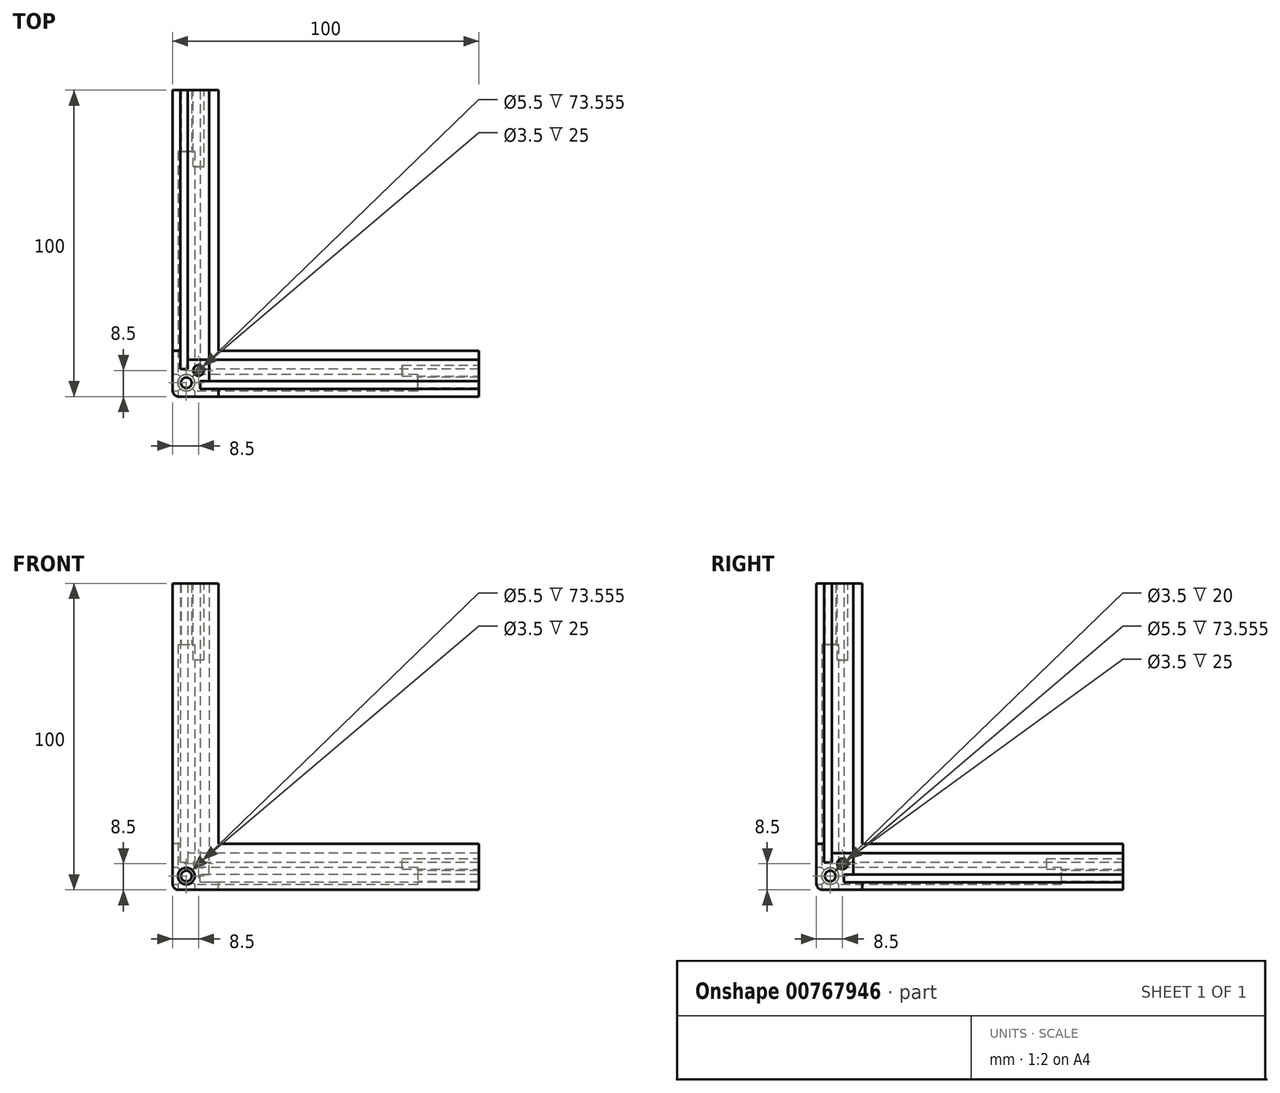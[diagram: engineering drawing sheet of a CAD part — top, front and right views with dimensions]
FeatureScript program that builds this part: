
annotation { "Feature Type Name" : "Feature", "Feature Type Description" : "" }
export const myFeature = defineFeature(function(context is Context, id is Id, definition is map)
    precondition{}
    {
        {
            var Q0;
            Q0=qCreatedBy(makeId("Top.planeOp"),FACE);
            var sketch = newSketch(context, id + "F0", { "sketchPlane" : qUnion([Q0])});
            skLineSegment(sketch, "E0", {"start": v(0, 15) * mm, "end": v(0, 0) * mm});
            skLineSegment(sketch, "E1", {"start": v(0, 0) * mm, "end": v(15, 0) * mm});
            skLineSegment(sketch, "E2", {"start": v(15, 0) * mm, "end": v(15, 2.5) * mm});
            skLineSegment(sketch, "E3", {"start": v(15, 2.5) * mm, "end": v(9, 2.5) * mm});
            skLineSegment(sketch, "E4", {"start": v(9, 2.5) * mm, "end": v(9, 5) * mm});
            skLineSegment(sketch, "E5", {"start": v(9, 5) * mm, "end": v(12, 5) * mm});
            skLineSegment(sketch, "E6", {"start": v(12, 5) * mm, "end": v(12, 12) * mm});
            skLineSegment(sketch, "E7", {"start": v(12, 12) * mm, "end": v(5, 12) * mm});
            skLineSegment(sketch, "E8", {"start": v(5, 12) * mm, "end": v(5, 9) * mm});
            skLineSegment(sketch, "E9", {"start": v(5, 9) * mm, "end": v(2.5, 9) * mm});
            skLineSegment(sketch, "E10", {"start": v(2.5, 9) * mm, "end": v(2.5, 15) * mm});
            skLineSegment(sketch, "E11", {"start": v(2.5, 15) * mm, "end": v(0, 15) * mm});
            skLineSegment(sketch, "E12", {"start": v(9, 5) * mm, "end": v(9, 9) * mm, "construction": true});
            skLineSegment(sketch, "E13", {"start": v(9, 9) * mm, "end": v(5, 9) * mm, "construction": true});
            skLineSegment(sketch, "E14", {"start": v(2.5, 9) * mm, "end": v(0, 9) * mm, "construction": true});
            skLineSegment(sketch, "E15", {"start": v(9, 2.5) * mm, "end": v(9, 0) * mm, "construction": true});
            skLineSegment(sketch, "E16", {"start": v(9, 0) * mm, "end": v(0, 9) * mm, "construction": true});
            skLineSegment(sketch, "E17", {"start": v(0, 0) * mm, "end": v(9, 9) * mm, "construction": true});
            skCircle(sketch, "E18", {"center": v(4.5, 4.5) * mm, "radius": 1.75 * mm});
            skSolve(sketch);
        }
        {
            var Q0;
            Q0=makeQuery(id+"F0.imprint","IMPRINT",FACE,{"disambiguationData":[TD([[makeQuery(id+"F0.imprint","IMPRINT",EDGE,{"derivedFrom":sQuery(id+"F0.wireOp",EDGE,"E0")}),1.0]])]});
            extrude(context, id + "F1", {"entities" : qUnion([Q0]), "depth" : 100 * mm, "offsetDistance" : 25 * mm});
        }
        {
            var Q0;
            Q0=qCreatedBy(makeId("Right.planeOp"),FACE);
            var sketch = newSketch(context, id + "F2", { "sketchPlane" : qUnion([Q0])});
            skLineSegment(sketch, "E19", {"start": v(0, 15) * mm, "end": v(0, 0) * mm});
            skLineSegment(sketch, "E20", {"start": v(0, 0) * mm, "end": v(15, 0) * mm});
            skLineSegment(sketch, "E21", {"start": v(15, 0) * mm, "end": v(15, 2.5) * mm});
            skLineSegment(sketch, "E22", {"start": v(15, 2.5) * mm, "end": v(9, 2.5) * mm});
            skLineSegment(sketch, "E23", {"start": v(9, 2.5) * mm, "end": v(9, 5) * mm});
            skLineSegment(sketch, "E24", {"start": v(9, 5) * mm, "end": v(12, 5) * mm});
            skLineSegment(sketch, "E25", {"start": v(12, 5) * mm, "end": v(12, 12) * mm});
            skLineSegment(sketch, "E26", {"start": v(12, 12) * mm, "end": v(5, 12) * mm});
            skLineSegment(sketch, "E27", {"start": v(5, 12) * mm, "end": v(5, 9) * mm});
            skLineSegment(sketch, "E28", {"start": v(5, 9) * mm, "end": v(2.5, 9) * mm});
            skLineSegment(sketch, "E29", {"start": v(2.5, 9) * mm, "end": v(2.5, 15) * mm});
            skLineSegment(sketch, "E30", {"start": v(2.5, 15) * mm, "end": v(0, 15) * mm});
            skLineSegment(sketch, "E31", {"start": v(9, 5) * mm, "end": v(9, 9) * mm, "construction": true});
            skLineSegment(sketch, "E32", {"start": v(9, 9) * mm, "end": v(5, 9) * mm, "construction": true});
            skLineSegment(sketch, "E33", {"start": v(2.5, 9) * mm, "end": v(0.02, 9) * mm, "construction": true});
            skLineSegment(sketch, "E34", {"start": v(9, 2.5) * mm, "end": v(9, 0) * mm, "construction": true});
            skLineSegment(sketch, "E35", {"start": v(9, 0) * mm, "end": v(0.02, 9) * mm, "construction": true});
            skLineSegment(sketch, "E36", {"start": v(0, 0) * mm, "end": v(9, 9) * mm, "construction": true});
            skCircle(sketch, "E37", {"center": v(4.5, 4.5) * mm, "radius": 1.75 * mm});
            skSolve(sketch);
        }
        {
            var Q0;
            Q0 = qSketchRegion(id + "F2", true);
            extrude(context, id + "F3", {"entities" : qUnion([Q0]), "operationType" : NewBodyOperationType.ADD, "depth" : 100 * mm, "offsetDistance" : 25 * mm});
        }
        {
            var Q0;
            Q0=qCreatedBy(makeId("Front.planeOp"),FACE);
            var sketch = newSketch(context, id + "F4", { "sketchPlane" : qUnion([Q0])});
            skLineSegment(sketch, "E38", {"start": v(0, 15) * mm, "end": v(0, 0) * mm});
            skLineSegment(sketch, "E39", {"start": v(0, 0) * mm, "end": v(15, 0) * mm});
            skLineSegment(sketch, "E40", {"start": v(15, 0) * mm, "end": v(15, 2.5) * mm});
            skLineSegment(sketch, "E41", {"start": v(15, 2.5) * mm, "end": v(9, 2.5) * mm});
            skLineSegment(sketch, "E42", {"start": v(9, 2.5) * mm, "end": v(9, 5) * mm});
            skLineSegment(sketch, "E43", {"start": v(9, 5) * mm, "end": v(12, 5) * mm});
            skLineSegment(sketch, "E44", {"start": v(12, 5) * mm, "end": v(12, 12) * mm});
            skLineSegment(sketch, "E45", {"start": v(12, 12) * mm, "end": v(5, 12) * mm});
            skLineSegment(sketch, "E46", {"start": v(5, 12) * mm, "end": v(5, 9) * mm});
            skLineSegment(sketch, "E47", {"start": v(5, 9) * mm, "end": v(2.5, 9) * mm});
            skLineSegment(sketch, "E48", {"start": v(2.5, 9) * mm, "end": v(2.5, 15) * mm});
            skLineSegment(sketch, "E49", {"start": v(2.5, 15) * mm, "end": v(0, 15) * mm});
            skLineSegment(sketch, "E50", {"start": v(9, 5) * mm, "end": v(9, 9) * mm, "construction": true});
            skLineSegment(sketch, "E51", {"start": v(9, 9) * mm, "end": v(5, 9) * mm, "construction": true});
            skLineSegment(sketch, "E52", {"start": v(2.5, 9) * mm, "end": v(0, 9) * mm, "construction": true});
            skLineSegment(sketch, "E53", {"start": v(9, 2.5) * mm, "end": v(9, 0) * mm, "construction": true});
            skLineSegment(sketch, "E54", {"start": v(9, 0) * mm, "end": v(0, 9) * mm, "construction": true});
            skLineSegment(sketch, "E55", {"start": v(0, 0) * mm, "end": v(9, 9) * mm, "construction": true});
            skCircle(sketch, "E56", {"center": v(4.5, 4.5) * mm, "radius": 1.75 * mm});
            skSolve(sketch);
        }
        {
            var Q0;
            Q0 = qSketchRegion(id + "F4", true);
            extrude(context, id + "F5", {"entities" : qUnion([Q0]), "operationType" : NewBodyOperationType.ADD, "oppositeDirection" : true, "depth" : 100 * mm, "offsetDistance" : 25 * mm});
        }
        {
            var Q0;
            {var subQ0=makeQuery(id+"F3.opExtrude","SWEPT_FACE",FACE,{"disambiguationData":[OSD([sQuery(id+"F2.wireOp",EDGE,"E25")])]});var subQ1=makeQuery(id+"F1.opExtrude","SWEPT_FACE",FACE,{"disambiguationData":[OSD([sQuery(id+"F0.wireOp",EDGE,"E7")])]});Q0=makeQuery(id+"F5.boolean.opBoolean","SPLIT",FACE,{"disambiguationData":[TD([makeQuery(id+"F1.opExtrude","SWEPT_FACE",FACE,{"disambiguationData":[OSD([sQuery(id+"F0.wireOp",EDGE,"E10")])]})])],"derivedFrom":makeQuery(id+"F3.boolean.opBoolean","MERGE",FACE,{"derivedFrom":[subQ1,subQ0]})});}
            extrude(context, id + "F6", {"entities" : qUnion([Q0]), "operationType" : NewBodyOperationType.REMOVE, "oppositeDirection" : true, "depth" : 3 * mm, "offsetDistance" : 25 * mm});
        }
        {
            var Q0;
            Q0=makeQuery(id+"F5.boolean.opBoolean","SPLIT",FACE,{"disambiguationData":[TD([makeQuery(id+"F1.opExtrude","SWEPT_FACE",FACE,{"disambiguationData":[OSD([sQuery(id+"F0.wireOp",EDGE,"E3")])]})])],"derivedFrom":makeQuery(id+"F5.opExtrude","SWEPT_FACE",FACE,{"disambiguationData":[OSD([sQuery(id+"F4.wireOp",EDGE,"E44")])]})});
            extrude(context, id + "F7", {"entities" : qUnion([Q0]), "operationType" : NewBodyOperationType.REMOVE, "oppositeDirection" : true, "depth" : 3 * mm, "offsetDistance" : 25 * mm});
        }
        {
            var Q0;
            Q0=makeQuery(id+"F3.boolean.opBoolean","SPLIT",FACE,{"disambiguationData":[TD([makeQuery(id+"F3.opExtrude","SWEPT_FACE",FACE,{"disambiguationData":[OSD([sQuery(id+"F2.wireOp",EDGE,"E22")])]})])],"derivedFrom":makeQuery(id+"F1.opExtrude","SWEPT_FACE",FACE,{"disambiguationData":[OSD([sQuery(id+"F0.wireOp",EDGE,"E6")])]})});
            extrude(context, id + "F8", {"entities" : qUnion([Q0]), "operationType" : NewBodyOperationType.REMOVE, "oppositeDirection" : true, "depth" : 3 * mm, "offsetDistance" : 25 * mm});
        }
        {
            var Q0;
            Q0=makeQuery(id+"F5.boolean.opBoolean","MERGE",FACE,{"derivedFrom":[makeQuery(id+"F1.opExtrude","SWEPT_FACE",FACE,{"disambiguationData":[OSD([sQuery(id+"F0.wireOp",EDGE,"E0")])]}),makeQuery(id+"F5.opExtrude","SWEPT_FACE",FACE,{"disambiguationData":[OSD([sQuery(id+"F4.wireOp",EDGE,"E38")])]})]});
            var sketch = newSketch(context, id + "F9", { "sketchPlane" : qUnion([Q0])});
            skCircle(sketch, "E57", {"center": v(-4.5, 4.5) * mm, "radius": 2.75 * mm});
            skSolve(sketch);
        }
        {
            var Q0;
            Q0 = qSketchRegion(id + "F9", true);
            extrude(context, id + "F10", {"entities" : qUnion([Q0]), "operationType" : NewBodyOperationType.REMOVE, "oppositeDirection" : true, "depth" : 80 * mm, "offsetDistance" : 25 * mm});
        }
        {
            var Q0;
            Q0=makeQuery(id+"F5.boolean.opBoolean","MERGE",FACE,{"derivedFrom":[makeQuery(id+"F3.boolean.opBoolean","MERGE",FACE,{"derivedFrom":[makeQuery(id+"F1.opExtrude","CAP_FACE",FACE,{"disambiguationData":[OSD([sQuery(id+"F0.wireOp",EDGE,"E0"),sQuery(id+"F0.wireOp",EDGE,"E1"),sQuery(id+"F0.wireOp",EDGE,"E2"),sQuery(id+"F0.wireOp",EDGE,"E3"),sQuery(id+"F0.wireOp",EDGE,"E4"),sQuery(id+"F0.wireOp",EDGE,"E5"),sQuery(id+"F0.wireOp",EDGE,"E6"),sQuery(id+"F0.wireOp",EDGE,"E7"),sQuery(id+"F0.wireOp",EDGE,"E8"),sQuery(id+"F0.wireOp",EDGE,"E9"),sQuery(id+"F0.wireOp",EDGE,"E10"),sQuery(id+"F0.wireOp",EDGE,"E11"),sQuery(id+"F0.wireOp",EDGE,"E18")])],"isStart":true}),makeQuery(id+"F3.opExtrude","SWEPT_FACE",FACE,{"disambiguationData":[OSD([sQuery(id+"F2.wireOp",EDGE,"E20")])]})]}),makeQuery(id+"F5.opExtrude","SWEPT_FACE",FACE,{"disambiguationData":[OSD([sQuery(id+"F4.wireOp",EDGE,"E39")])]})]});
            var sketch = newSketch(context, id + "F11", { "sketchPlane" : qUnion([Q0])});
            skCircle(sketch, "E58", {"center": v(4.5, -4.5) * mm, "radius": 2.75 * mm});
            skSolve(sketch);
        }
        {
            var Q0;
            Q0 = qSketchRegion(id + "F11", true);
            extrude(context, id + "F12", {"entities" : qUnion([Q0]), "operationType" : NewBodyOperationType.REMOVE, "oppositeDirection" : true, "depth" : 80 * mm, "offsetDistance" : 25 * mm});
        }
        {
            var Q0;
            Q0=makeQuery(id+"F3.boolean.opBoolean","MERGE",FACE,{"derivedFrom":[makeQuery(id+"F1.opExtrude","SWEPT_FACE",FACE,{"disambiguationData":[OSD([sQuery(id+"F0.wireOp",EDGE,"E1")])]}),makeQuery(id+"F3.opExtrude","SWEPT_FACE",FACE,{"disambiguationData":[OSD([sQuery(id+"F2.wireOp",EDGE,"E19")])]})]});
            var sketch = newSketch(context, id + "F13", { "sketchPlane" : qUnion([Q0])});
            skCircle(sketch, "E59", {"center": v(4.5, 4.5) * mm, "radius": 2.75 * mm});
            skSolve(sketch);
        }
        {
            var Q0;
            Q0 = qSketchRegion(id + "F13", true);
            extrude(context, id + "F14", {"entities" : qUnion([Q0]), "operationType" : NewBodyOperationType.REMOVE, "oppositeDirection" : true, "depth" : 80 * mm, "offsetDistance" : 25 * mm});
        }
        {
            var Q0;
            Q0=makeQuery(id+"F5.boolean.opBoolean","MERGE",EDGE,{"derivedFrom":[makeQuery(id+"F1.opExtrude","CAP_EDGE",EDGE,{"disambiguationData":[OSD([sQuery(id+"F0.wireOp",EDGE,"E0")])],"isStart":true}),makeQuery(id+"F5.opExtrude","SWEPT_EDGE",EDGE,{"disambiguationData":[OSD([sQuery(id+"F4.wireOp",EDGE,"E38"),sQuery(id+"F4.wireOp",EDGE,"E39")])]})]});
            var Q1;
            Q1=makeQuery(id+"F3.boolean.opBoolean","MERGE",EDGE,{"derivedFrom":[makeQuery(id+"F1.opExtrude","CAP_EDGE",EDGE,{"disambiguationData":[OSD([sQuery(id+"F0.wireOp",EDGE,"E1")])],"isStart":true}),makeQuery(id+"F3.opExtrude","SWEPT_EDGE",EDGE,{"disambiguationData":[OSD([sQuery(id+"F2.wireOp",EDGE,"E19"),sQuery(id+"F2.wireOp",EDGE,"E20")])]})]});
            var Q2;
            Q2=makeQuery(id+"F1.opExtrude","SWEPT_EDGE",EDGE,{"disambiguationData":[OSD([sQuery(id+"F0.wireOp",EDGE,"E0"),sQuery(id+"F0.wireOp",EDGE,"E1")])]});
            fillet(context, id + "F15", {"entities" : qUnion([Q0, Q1, Q2]), "radius" : 2 * mm, "tangentPropagation" : true, "allowEdgeOverflow" : false});
        }
        {
            var Q0;
            Q0=makeQuery(id+"F3.opExtrude","CAP_FACE",FACE,{"disambiguationData":[OSD([sQuery(id+"F2.wireOp",EDGE,"E19"),sQuery(id+"F2.wireOp",EDGE,"E20"),sQuery(id+"F2.wireOp",EDGE,"E21"),sQuery(id+"F2.wireOp",EDGE,"E22"),sQuery(id+"F2.wireOp",EDGE,"E23"),sQuery(id+"F2.wireOp",EDGE,"E24"),sQuery(id+"F2.wireOp",EDGE,"E25"),sQuery(id+"F2.wireOp",EDGE,"E26"),sQuery(id+"F2.wireOp",EDGE,"E27"),sQuery(id+"F2.wireOp",EDGE,"E28"),sQuery(id+"F2.wireOp",EDGE,"E29"),sQuery(id+"F2.wireOp",EDGE,"E30"),sQuery(id+"F2.wireOp",EDGE,"E37")])],"isStart":false});
            var sketch = newSketch(context, id + "F16", { "sketchPlane" : qUnion([Q0])});
            skCircle(sketch, "E60", {"center": v(8.5, 8.5) * mm, "radius": 1.75 * mm});
            skLineSegment(sketch, "E61", {"start": v(12, 5) * mm, "end": v(5, 12) * mm, "construction": true});
            skLineSegment(sketch, "E62", {"start": v(12, 12) * mm, "end": v(8.5, 8.5) * mm, "construction": true});
            skSolve(sketch);
        }
        {
            var Q0;
            Q0 = qSketchRegion(id + "F16", true);
            extrude(context, id + "F17", {"entities" : qUnion([Q0]), "operationType" : NewBodyOperationType.REMOVE, "oppositeDirection" : true, "depth" : 25 * mm, "offsetDistance" : 25 * mm});
        }
        {
            var Q0;
            Q0=makeQuery(id+"F1.opExtrude","CAP_FACE",FACE,{"disambiguationData":[OSD([sQuery(id+"F0.wireOp",EDGE,"E0"),sQuery(id+"F0.wireOp",EDGE,"E1"),sQuery(id+"F0.wireOp",EDGE,"E2"),sQuery(id+"F0.wireOp",EDGE,"E3"),sQuery(id+"F0.wireOp",EDGE,"E4"),sQuery(id+"F0.wireOp",EDGE,"E5"),sQuery(id+"F0.wireOp",EDGE,"E6"),sQuery(id+"F0.wireOp",EDGE,"E7"),sQuery(id+"F0.wireOp",EDGE,"E8"),sQuery(id+"F0.wireOp",EDGE,"E9"),sQuery(id+"F0.wireOp",EDGE,"E10"),sQuery(id+"F0.wireOp",EDGE,"E11"),sQuery(id+"F0.wireOp",EDGE,"E18")])],"isStart":false});
            var sketch = newSketch(context, id + "F18", { "sketchPlane" : qUnion([Q0])});
            skLineSegment(sketch, "E63", {"start": v(12, 5) * mm, "end": v(5, 12) * mm, "construction": true});
            skLineSegment(sketch, "E64", {"start": v(5, 12) * mm, "end": v(12, 12) * mm});
            skLineSegment(sketch, "E65", {"start": v(12, 12) * mm, "end": v(8.5, 8.5) * mm, "construction": true});
            skCircle(sketch, "E66", {"center": v(8.5, 8.5) * mm, "radius": 1.75 * mm});
            skSolve(sketch);
        }
        {
            var Q0;
            Q0=makeQuery(id+"F18.imprint","IMPRINT",FACE,{"disambiguationData":[TD([[makeQuery(id+"F18.imprint","IMPRINT",EDGE,{"derivedFrom":sQuery(id+"F18.wireOp",EDGE,"E66")}),1.0]])]});
            extrude(context, id + "F19", {"entities" : qUnion([Q0]), "operationType" : NewBodyOperationType.REMOVE, "oppositeDirection" : true, "depth" : 25 * mm, "offsetDistance" : 25 * mm});
        }
        {
            var Q0;
            Q0=makeQuery(id+"F5.opExtrude","CAP_FACE",FACE,{"disambiguationData":[OSD([sQuery(id+"F4.wireOp",EDGE,"E38"),sQuery(id+"F4.wireOp",EDGE,"E39"),sQuery(id+"F4.wireOp",EDGE,"E40"),sQuery(id+"F4.wireOp",EDGE,"E41"),sQuery(id+"F4.wireOp",EDGE,"E42"),sQuery(id+"F4.wireOp",EDGE,"E43"),sQuery(id+"F4.wireOp",EDGE,"E44"),sQuery(id+"F4.wireOp",EDGE,"E45"),sQuery(id+"F4.wireOp",EDGE,"E46"),sQuery(id+"F4.wireOp",EDGE,"E47"),sQuery(id+"F4.wireOp",EDGE,"E48"),sQuery(id+"F4.wireOp",EDGE,"E49"),sQuery(id+"F4.wireOp",EDGE,"E56")])],"isStart":false});
            var sketch = newSketch(context, id + "F20", { "sketchPlane" : qUnion([Q0])});
            skLineSegment(sketch, "E67", {"start": v(-12, 5) * mm, "end": v(-5, 12) * mm, "construction": true});
            skLineSegment(sketch, "E68", {"start": v(-12, 12) * mm, "end": v(-8.5, 8.5) * mm, "construction": true});
            skCircle(sketch, "E69", {"center": v(-8.5, 8.5) * mm, "radius": 1.75 * mm});
            skSolve(sketch);
        }
        {
            var Q0;
            Q0=makeQuery(id+"F20.imprint","IMPRINT",FACE,{"disambiguationData":[TD([[makeQuery(id+"F20.imprint","IMPRINT",EDGE,{"derivedFrom":sQuery(id+"F20.wireOp",EDGE,"E69")}),1.0]])]});
            extrude(context, id + "F21", {"entities" : qUnion([Q0]), "operationType" : NewBodyOperationType.REMOVE, "oppositeDirection" : true, "depth" : 25 * mm, "offsetDistance" : 25 * mm});
        }
    });
